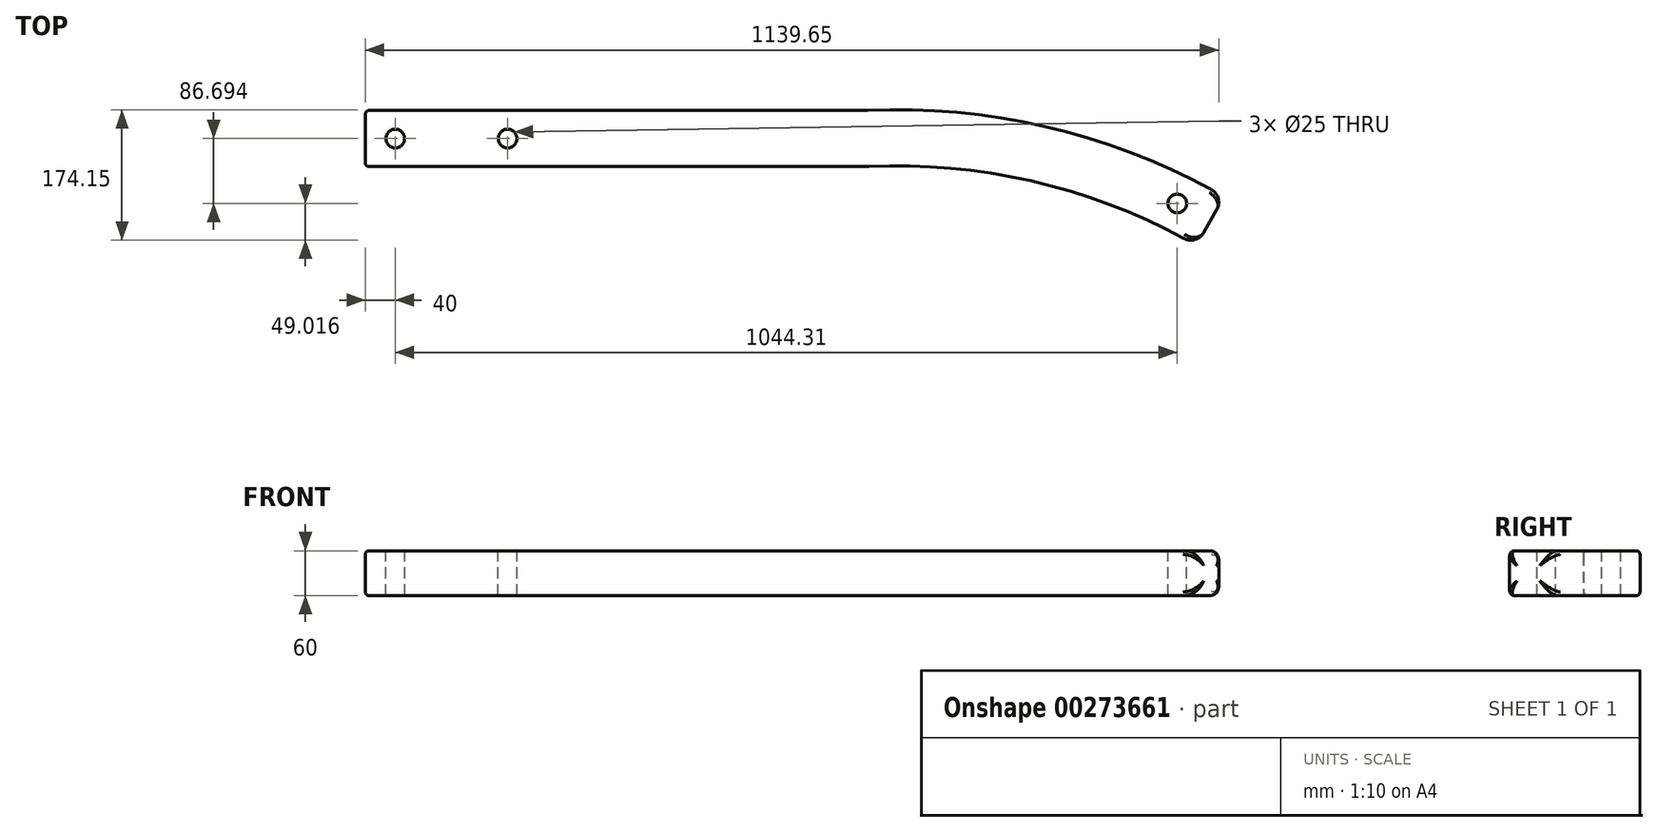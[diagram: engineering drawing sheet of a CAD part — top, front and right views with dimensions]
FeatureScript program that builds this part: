
annotation { "Feature Type Name" : "Feature", "Feature Type Description" : "" }
export const myFeature = defineFeature(function(context is Context, id is Id, definition is map)
    precondition{}
    {
        {
            var Q0;
            Q0=qCreatedBy(makeId("Top.planeOp"),FACE);
            var sketch = newSketch(context, id + "F0", { "sketchPlane" : qUnion([Q0])});
            skLineSegment(sketch, "E0.bottom", {"start": v(0, 0) * mm, "end": v(750, 0) * mm});
            skLineSegment(sketch, "E0.top", {"start": v(0, 75) * mm, "end": v(750, 75) * mm});
            skLineSegment(sketch, "E0.left", {"start": v(0, 0) * mm, "end": v(0, 75) * mm});
            skLineSegment(sketch, "E0.right", {"start": v(750, 0) * mm, "end": v(750, 75) * mm});
            skPoint(sketch, "E1.second.point", {"position": v(750, -1599.78) * mm});
            skPoint(sketch, "E1.third.point", {"position": v(1510.87, -841.84) * mm});
            skArc(sketch, "E2.0", {"start": v(1147.07, -40.25) * mm, "mid": v(917, 51.4) * mm, "end": v(670.49, 75) * mm});
            skLineSegment(sketch, "E3", {"start": v(1109.74, -105.3) * mm, "end": v(1147.07, -40.25) * mm});
            skArc(sketch, "E4.trimOffspring", {"start": v(1109.74, -105.3) * mm, "mid": v(898.55, -21.3) * mm, "end": v(672.27, 0) * mm});
            skSolve(sketch);
        }
        {
            var Q0;
            {var subQ0=sQuery(id+"F0.wireOp",EDGE,"E0.left");Q0=makeQuery(id+"F0.imprint","IMPRINT",FACE,{"disambiguationData":[TD([[makeQuery(id+"F0.imprint","IMPRINT",EDGE,{"derivedFrom":subQ0}),-1.0]])]});}
            var Q1;
            {var subQ2=sQuery(id+"F0.wireOp",EDGE,"E0.right");Q1=makeQuery(id+"F0.imprint","IMPRINT",FACE,{"disambiguationData":[TD([[makeQuery(id+"F0.imprint","IMPRINT",EDGE,{"derivedFrom":subQ2}),-1.0]])]});}
            extrude(context, id + "F1", {"entities" : qUnion([Q0, Q1]), "depth" : 60 * mm});
        }
        {
            var Q0;
            Q0=makeQuery(id+"F1.opExtrude","CAP_EDGE",EDGE,{"disambiguationData":[OSD([sQuery(id+"F0.wireOp",EDGE,"E4.trimOffspring")])],"isStart":true});
            var Q1;
            Q1=makeQuery(id+"F1.opExtrude","CAP_EDGE",EDGE,{"disambiguationData":[OSD([sQuery(id+"F0.wireOp",EDGE,"E2.0")])],"isStart":true});
            var Q2;
            Q2=makeQuery(id+"F1.opExtrude","CAP_EDGE",EDGE,{"disambiguationData":[OSD([sQuery(id+"F0.wireOp",EDGE,"E2.0")])],"isStart":false});
            var Q3;
            Q3=makeQuery(id+"F1.opExtrude","CAP_EDGE",EDGE,{"disambiguationData":[OSD([sQuery(id+"F0.wireOp",EDGE,"E0.top")])],"isStart":false});
            var Q4;
            Q4=makeQuery(id+"F1.opExtrude","CAP_EDGE",EDGE,{"disambiguationData":[OSD([sQuery(id+"F0.wireOp",EDGE,"E0.top")])],"isStart":true});
            var Q5;
            Q5=makeQuery(id+"F1.opExtrude","CAP_EDGE",EDGE,{"disambiguationData":[OSD([sQuery(id+"F0.wireOp",EDGE,"E0.bottom")])],"isStart":true});
            var Q6;
            Q6=makeQuery(id+"F1.opExtrude","SWEPT_EDGE",EDGE,{"disambiguationData":[OSD([sQuery(id+"F0.wireOp",EDGE,"E0.bottom"),sQuery(id+"F0.wireOp",EDGE,"E4.trimOffspring")])]});
            var Q7;
            Q7=makeQuery(id+"F1.opExtrude","SWEPT_EDGE",EDGE,{"disambiguationData":[OSD([sQuery(id+"F0.wireOp",EDGE,"E0.top"),sQuery(id+"F0.wireOp",EDGE,"E2.0")])]});
            var Q8;
            Q8=makeQuery(id+"F1.opExtrude","CAP_EDGE",EDGE,{"disambiguationData":[OSD([sQuery(id+"F0.wireOp",EDGE,"E0.bottom")])],"isStart":false});
            var Q9;
            Q9=makeQuery(id+"F1.opExtrude","CAP_EDGE",EDGE,{"disambiguationData":[OSD([sQuery(id+"F0.wireOp",EDGE,"E4.trimOffspring")])],"isStart":false});
            var Q10;
            Q10=makeQuery(id+"F1.opExtrude","SWEPT_EDGE",EDGE,{"disambiguationData":[OSD([sQuery(id+"F0.wireOp",EDGE,"E0.top"),sQuery(id+"F0.wireOp",EDGE,"E0.left")])]});
            var Q11;
            Q11=makeQuery(id+"F1.opExtrude","CAP_EDGE",EDGE,{"disambiguationData":[OSD([sQuery(id+"F0.wireOp",EDGE,"E0.left")])],"isStart":false});
            var Q12;
            Q12=makeQuery(id+"F1.opExtrude","SWEPT_EDGE",EDGE,{"disambiguationData":[OSD([sQuery(id+"F0.wireOp",EDGE,"E0.bottom"),sQuery(id+"F0.wireOp",EDGE,"E0.left")])]});
            var Q13;
            Q13=makeQuery(id+"F1.opExtrude","CAP_EDGE",EDGE,{"disambiguationData":[OSD([sQuery(id+"F0.wireOp",EDGE,"E0.left")])],"isStart":true});
            fillet(context, id + "F2", {"entities" : qUnion([Q0, Q1, Q2, Q3, Q4, Q5, Q6, Q7, Q8, Q9, Q10, Q11, Q12, Q13]), "radius" : 5 * mm, "tangentPropagation" : true, "allowEdgeOverflow" : false});
        }
        {
            var Q0;
            Q0=makeQuery(id+"F1.opExtrude","SWEPT_EDGE",EDGE,{"disambiguationData":[OSD([sQuery(id+"F0.wireOp",EDGE,"E2.0"),sQuery(id+"F0.wireOp",EDGE,"E3")])]});
            fillet(context, id + "F3", {"entities" : qUnion([Q0]), "radius" : 20 * mm, "tangentPropagation" : true, "allowEdgeOverflow" : false});
        }
        {
            var Q0;
            Q0=makeQuery(id+"F1.opExtrude","CAP_FACE",FACE,{"disambiguationData":[OSD([sQuery(id+"F0.wireOp",EDGE,"E0.bottom"),sQuery(id+"F0.wireOp",EDGE,"E0.top"),sQuery(id+"F0.wireOp",EDGE,"E0.left"),sQuery(id+"F0.wireOp",EDGE,"E2.0"),sQuery(id+"F0.wireOp",EDGE,"E3"),sQuery(id+"F0.wireOp",EDGE,"E4.trimOffspring")])],"isStart":false});
            var sketch = newSketch(context, id + "F4", { "sketchPlane" : qUnion([Q0])});
            skCircle(sketch, "E5", {"center": v(40, 37.5) * mm, "radius": 12.5 * mm});
            skCircle(sketch, "E6", {"center": v(190, 37.5) * mm, "radius": 12.5 * mm});
            skCircle(sketch, "E7", {"center": v(1084.3, -49.2) * mm, "radius": 12.5 * mm});
            skSolve(sketch);
        }
        {
            var Q0;
            Q0=makeQuery(id+"F4.imprint","IMPRINT",FACE,{"disambiguationData":[TD([[makeQuery(id+"F4.imprint","IMPRINT",EDGE,{"derivedFrom":sQuery(id+"F4.wireOp",EDGE,"E7")}),1.0]])]});
            var Q1;
            Q1=makeQuery(id+"F4.imprint","IMPRINT",FACE,{"disambiguationData":[TD([[makeQuery(id+"F4.imprint","IMPRINT",EDGE,{"derivedFrom":sQuery(id+"F4.wireOp",EDGE,"E6")}),1.0]])]});
            var Q2;
            Q2=makeQuery(id+"F4.imprint","IMPRINT",FACE,{"disambiguationData":[TD([[makeQuery(id+"F4.imprint","IMPRINT",EDGE,{"derivedFrom":sQuery(id+"F4.wireOp",EDGE,"E5")}),1.0]])]});
            extrude(context, id + "F5", {"entities" : qUnion([Q0, Q1, Q2]), "operationType" : NewBodyOperationType.REMOVE, "endBound" : BoundingType.THROUGH_ALL, "oppositeDirection" : true, "depth" : 25 * mm});
        }
    });
